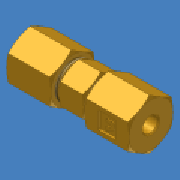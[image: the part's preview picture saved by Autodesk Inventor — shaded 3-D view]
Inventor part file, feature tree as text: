
AUTODESK INVENTOR PART (.ipt)
format: ipt  version: 2016 SP1 (Build 200210100, 210)  size: 289,280 bytes
history: native  units: in
note: dims shown in document units (in); Inventor stores cm internally (conversion verified against a paired STEP export)
features: other x2, sketch x1, imported_body x1
ambient origin geometry x8: Origin, YZ Plane, XZ Plane, XY Plane, X Axis, Y Axis, Z Axis, Center Point
bodies: Solid1 (feature_tree)
feature tree (4):
  other  "Table"
  other  "Union 62C.ipt"
  sketch  "Sketch1"
  imported_body  "DerivedBody::Union 62C.ipt"
